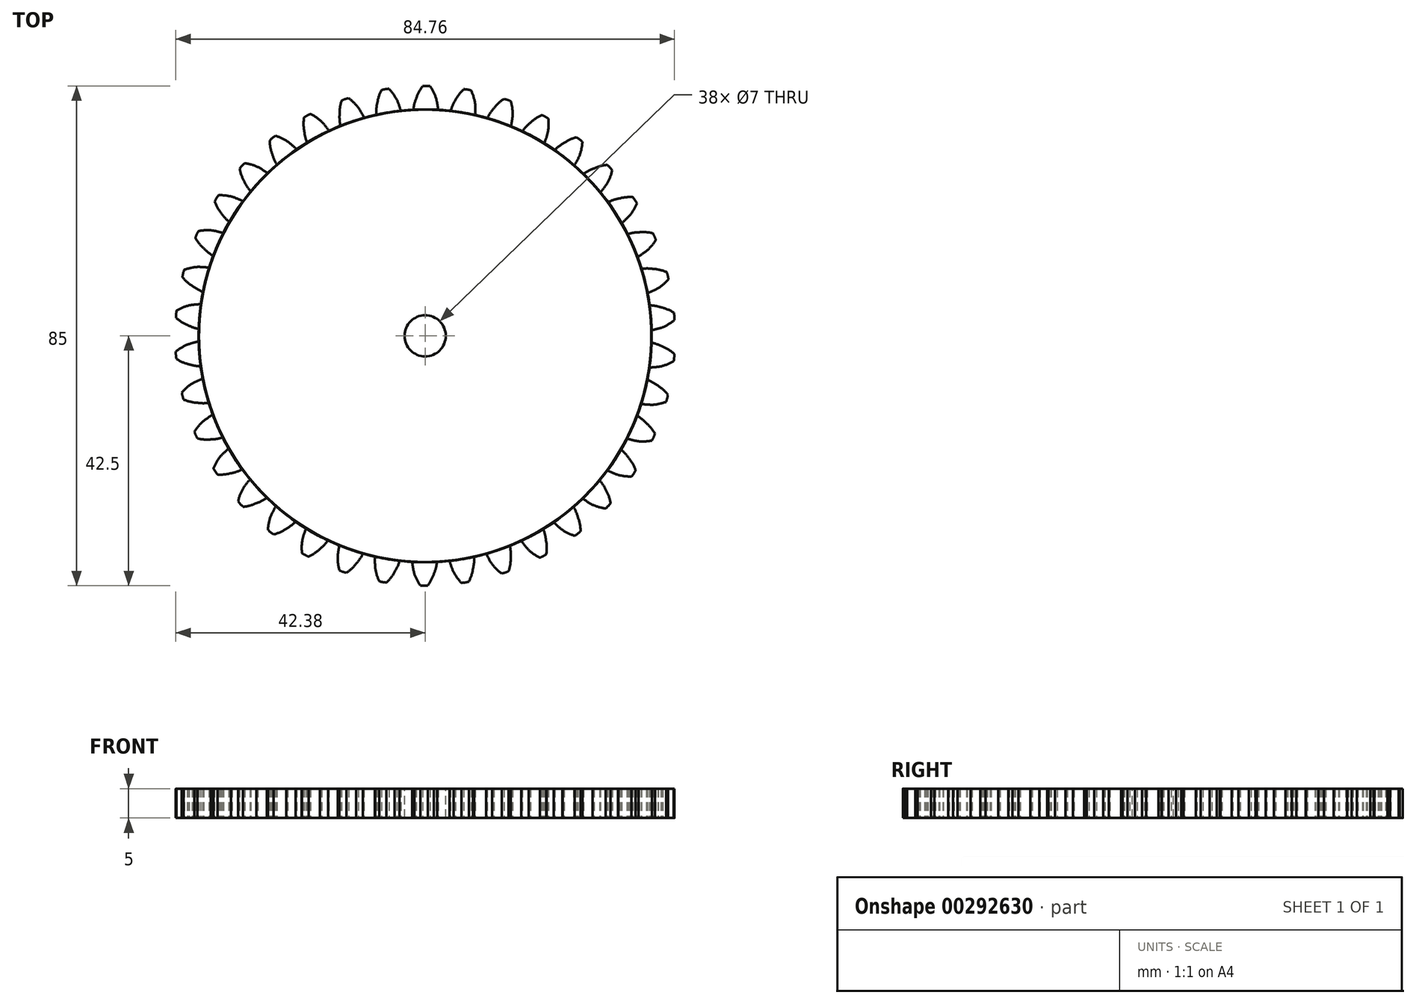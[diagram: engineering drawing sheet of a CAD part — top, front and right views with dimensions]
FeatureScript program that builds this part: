
annotation { "Feature Type Name" : "Feature", "Feature Type Description" : "" }
export const myFeature = defineFeature(function(context is Context, id is Id, definition is map)
    precondition{}
    {
        {
            var Q0;
            Q0=qCreatedBy(makeId("Top.planeOp"),FACE);
            var sketch = newSketch(context, id + "F0", { "sketchPlane" : qUnion([Q0])});
            skCircle(sketch, "E0", {"center": v(0, 0) * mm, "radius": 38.5 * mm});
            skCircle(sketch, "E1", {"center": v(0, 0) * mm, "radius": 38.5 * mm, "construction": true});
            skCircle(sketch, "E2", {"center": v(0, 0) * mm, "radius": 40.5 * mm, "construction": true});
            skLineSegment(sketch, "E3", {"start": v(0, 0) * mm, "end": v(0, 45.22) * mm, "construction": true});
            skLineSegment(sketch, "E4", {"start": v(0, 38.5) * mm, "end": v(-2, 38.5) * mm, "construction": true});
            skLineSegment(sketch, "E5", {"start": v(0, 38.5) * mm, "end": v(2, 38.5) * mm, "construction": true});
            skCircle(sketch, "E6", {"center": v(0, 0) * mm, "radius": 42.5 * mm, "construction": true});
            skArc(sketch, "E7", {"start": v(2.22, 38.44) * mm, "mid": v(2.07, 39.42) * mm, "end": v(1.86, 40.4) * mm});
            skArc(sketch, "E8", {"start": v(1.85, 40.41) * mm, "mid": v(1.41, 41.47) * mm, "end": v(0.83, 42.46) * mm});
            skLineSegment(sketch, "E9", {"start": v(1.85, 40.41) * mm, "end": v(1.86, 40.4) * mm});
            skArc(sketch, "E10", {"start": v(0.83, 42.46) * mm, "mid": v(0.2, 42.5) * mm, "end": v(-0.43, 42.46) * mm});
            skArc(sketch, "E11.trimOffspring", {"start": v(-0.43, 42.46) * mm, "mid": v(-1.06, 41.49) * mm, "end": v(-1.5, 40.42) * mm});
            skArc(sketch, "E12", {"start": v(-1.5, 40.42) * mm, "mid": v(-1.83, 39.45) * mm, "end": v(-2.02, 38.45) * mm});
            skSolve(sketch);
        }
        {
            var Q0;
            Q0 = qSketchRegion(id + "F0", true);
            extrude(context, id + "F1", {"entities" : qUnion([Q0]), "depth" : 5 * mm});
        }
        {
            var Q0;
            Q0=makeQuery(id+"F1.opExtrude","SWEPT_BODY",BODY,{"disambiguationData":[OSD([sQuery(id+"F0.wireOp",EDGE,"E0"),sQuery(id+"F0.wireOp",EDGE,"2l8b5inm-9n9V-LjoX-rjHo-bNHDnOOvV7YF"),sQuery(id+"F0.wireOp",EDGE,"hnoPwsaR-hyT5-JONm-qnpl-nOTiw0M5PYfl"),sQuery(id+"F0.wireOp",EDGE,"o5D4qyzc-6s9J-wgQI-WI57-7Jy8VC7K6sDE")])]});
            var Q1;
            Q1=makeQuery(id+"F1.opExtrude","SWEPT_FACE",FACE,{"disambiguationData":[OSD([sQuery(id+"F0.wireOp",EDGE,"E0")])]});
            circularPattern(context, id + "F2", {"entities" : qUnion([Q0]), "axis" : qUnion([Q1]), "angle" : 360 * degree, "instanceCount" : 38, "equalSpace" : true});
        }
        {
            var Q0;
            Q0=makeQuery(id+"F1.opExtrude","CAP_FACE",FACE,{"disambiguationData":[OSD([sQuery(id+"F0.wireOp",EDGE,"E0"),sQuery(id+"F0.wireOp",EDGE,"2l8b5inm-9n9V-LjoX-rjHo-bNHDnOOvV7YF"),sQuery(id+"F0.wireOp",EDGE,"hnoPwsaR-hyT5-JONm-qnpl-nOTiw0M5PYfl"),sQuery(id+"F0.wireOp",EDGE,"o5D4qyzc-6s9J-wgQI-WI57-7Jy8VC7K6sDE")])],"isStart":false});
            var sketch = newSketch(context, id + "F3", { "sketchPlane" : qUnion([Q0])});
            skPoint(sketch, "E13.middle", {"position": v(0, 0) * mm});
            skCircle(sketch, "E14", {"center": v(0, 0) * mm, "radius": 3.5 * mm});
            skSolve(sketch);
        }
        {
            var Q0;
            Q0 = qSketchRegion(id + "F3", true);
            extrude(context, id + "F4", {"entities" : qUnion([Q0]), "operationType" : NewBodyOperationType.REMOVE, "endBound" : BoundingType.SYMMETRIC, "oppositeDirection" : true, "depth" : 25 * mm});
        }
    });
